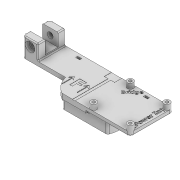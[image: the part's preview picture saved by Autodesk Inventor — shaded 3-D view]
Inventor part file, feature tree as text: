
AUTODESK INVENTOR PART (.ipt)
format: ipt  version: 2022 (Build 260153000, 153)  size: 787,968 bytes
history: native  units: mm
features: extrude x15, sketch x15, reference x9, fillet x4, projected_geometry x4, other x4, plane x2, pattern_linear x1
ambient origin geometry x8: Origin, YZ Plane, XZ Plane, XY Plane, X Axis, Y Axis, Z Axis, Center Point
bodies: Volumenkörper1 (feature_tree)
feature tree (54):
  extrude  "Extrusion1"  Depth=20.0mm TaperAngle=0.0deg
  extrude  "Extrusion2"  Depth=16.0mm TaperAngle=0.0deg
  extrude  "Extrusion8"  Depth=47.0mm
  fillet  "Rundung4"  Radius=4.0mm
  sketch  "Skizze11"  dims[d50=7.05mm d51=7.05mm]
  plane  "Arbeitsebene3"
  extrude  "Extrusion9"  Depth=7.05mm
  sketch  "Skizze12"  dims[d52=3.0mm d53=4.875mm d54=4.875mm d55=10.0mm d56=0.0mm]
  plane  "Arbeitsebene4"
  extrude  "Extrusion10"  Depth=4.875mm
  fillet  "Rundung5"  Radius=4.875mm
  fillet  "Rundung6"  Radius=10.0mm
  extrude  "Extrusion11"  Depth=1.0mm
  extrude  "Extrusion12"  Depth=5.7mm
  extrude  "Extrusion13"  Depth=9.2mm
  extrude  "Extrusion14"  Depth=3.5mm TaperAngle=0.0deg
  pattern_linear  "Rechteckige Anordnung2"  Count1=2 Spacing1=36.0mm
  extrude  "Extrusion15"  Depth=0.2mm TaperAngle=0.0deg
  extrude  "Extrusion16"  TaperAngle=0.0deg  [1 undecoded]
  extrude  "Extrusion17"  Depth=10.0mm
  fillet  "Rundung7"  Radius=17.0mm
  extrude  "Extrusion18"  Depth=2.0mm
  extrude  "Extrusion19"  Depth=4.0mm
  extrude  "Extrusion20"  Depth=11.0mm TaperAngle=0.0deg
  sketch  "Skizze1"  dims[d0=48.0mm d1=20.0mm d2=0.0mm]
  sketch  "Skizze2"  dims[d3=5.2mm d4=16.0mm d5=0.0mm]
  sketch  "Skizze10"  dims[d46=21.0mm d47=47.0mm d48=4.0mm d49=0.0mm]
  reference  "Referenz5"
  reference  "Referenz6"
  reference  "Referenz7"
  reference  "Referenz8"
  reference  "Referenz9"
  reference  "Referenz10"
  reference  "Referenz11"
  reference  "Referenz12"
  projected_geometry  "Projizierte Kontur1"
  sketch  "Skizze13"  dims[d57=10.0mm d58=0.0mm d59=1.0mm]
  reference  "Referenz13"
  sketch  "Skizze14"  dims[d60=1.0mm d61=5.7mm]
  sketch  "Skizze15"  dims[d62=3.0mm d63=0.0mm d64=9.2mm]
  sketch  "Skizze16"  dims[d65=3.5mm d66=0.0mm d67=3.5mm d68=0.0mm]
  sketch  "Skizze17"  dims[d69=2.9mm]
  sketch  "Skizze18"  dims[d70=6.0mm]
  projected_geometry  "Projizierte Kontur2"
  projected_geometry  "Projizierte Kontur3"
  sketch  "Skizze19"  dims[d71=3.0mm]
  projected_geometry  "Projizierte Kontur4"
  sketch  "Skizze20"  dims[d72=3.0mm]
  sketch  "Skizze21"  dims[d73=5.0mm d74=0.0mm d75=20.0mm d77=36.0mm]
  sketch  "Skizze22"  dims[d78=20.0mm d80=36.0mm d81=0.2mm d82=0.0mm d83=0.0mm d84=0.0mm d85=10.0mm d86=17.0mm d87=0.0mm d88=2.0mm d89=4.0mm d90=11.0mm d91=0.0mm d92=4.0mm d93=4.0mm d94=2.0mm d95=30.0mm d96=30.0mm d97=3.0mm d98=11.0mm d99=0.0mm d100=0.2mm d101=0.0mm]
  other  "<userpath>\SynologyDrive\WiMi\Projekte\HeleneRoboterarm\KraftMessNadelv2\Gesamt.iam"
  other  "Gesamt.iam"
  other  "micro load cell CZL635:1"
  other  "NadelHalterLose:1"
note: 1 required parameter value undecoded (feature->parameter linkage not recoverable at this tier; creation-order binding heuristic only, values carry confidence <= 0.55)
